# Revit family: TEMID_Шлагбаум_BGM2000L-4M
name_source: partatom
category: Охранная сигнализация
units: mm (PartAtom-declared; Revit-internal decimal feet)

## family parameters
Всегда вертикально = Нет
На основе рабочей плоскости = Нет
Общий = Да
При загрузке вырезать с полостями = Нет
Размер круглого соединителя = Использовать диаметр
Сохранять ориентацию аннотаций = Нет
Тип детали = Нормальный
Точка расчета площади = Да

## types (1)
- BGM2000L-4M_Стрела_Левая_Подъём стандарт_Стрела 4 м
    =Габариты= = =Габариты=
    =Стрела= = =Стрела=
    ADSK_Единица измерения = шт.
    ADSK_Завод-изготовитель = TEMID
    ADSK_Классификация нагрузок = Прочее
    ADSK_Количество = 1
    ADSK_Количество фаз = 1
    ADSK_Коэффициент мощности = 0.95
    ADSK_Марка = BGM2000L-4M
    ADSK_Наименование = Шлагбаум электромеханический со стрелой 4м мягкая, бесщеточный двигатель 24 В пост. тока, комплект: стрела 4 м мягкая, механизм откидывания стрелы, время подъема 1,5 c, 220 В, с блоком управления, р/канал, подсветка шлагбаума, Bluetooth, APP ZKBarrier., левый
    ADSK_Напряжение = 220 В
    ADSK_Номинальная мощность = 100 Вт
    ADSK_Обозначение = RD
    ADSK_Полная мощность = 105 В·А
    ADSK_Раздел спецификации = 3. Периферийное оборудование
    ADSK_Размер_Высота = 1070 мм
    ADSK_Размер_Глубина = 306 мм
    ADSK_Размер_Ширина = 350 мм
    ADSK_Тип = BGM2000L-4M
    ADSK_Ток = 478.469 мА
    URL = https://temid-global.ru
    Зона обслуживания_Отступ от прибора = 250 мм
    Материал боковины стрелы = Красный
    Материал буквы_Стрела закрыта = Красный
    Материал буквы_Стрела открыта = Голубой
    Материал стойки = Серый
    Материал стрелы = Красно белая клетка
    Отметка по умолчанию = 0 мм
    Стрела основание_Высота = 150 мм
    Стрела основание_Глубина = 50 мм
    Стрела основание_Ширина = 150 мм
    Стрела подъём Г образный = Нет
    Стрела подъём стандартный = Да
    Стрела_Высота снования = 700 мм
    Стрела_Глубина = 40 мм
    Стрела_Длина 1 участка = 60 мм
    Стрела_Длина 2 участка = 3620 мм
    Стрела_Длина общая = 4000 мм
    Стрела_Левая = Да
    Стрела_Правая = Нет
    Стрела_Ширина = 50 мм
    УГО_Тип = УГО_СС_Универсальный_текст_прямоугольный : УГО_СС_Шлагбаум
    Угол 1_закрытой стрелы = 270.00°
    Угол 1_открытой стрелы = 180.00°
    Угол 2_закрытой стрелы = 90.00°
    Угол 2_открытой стрелы = 90.00°
